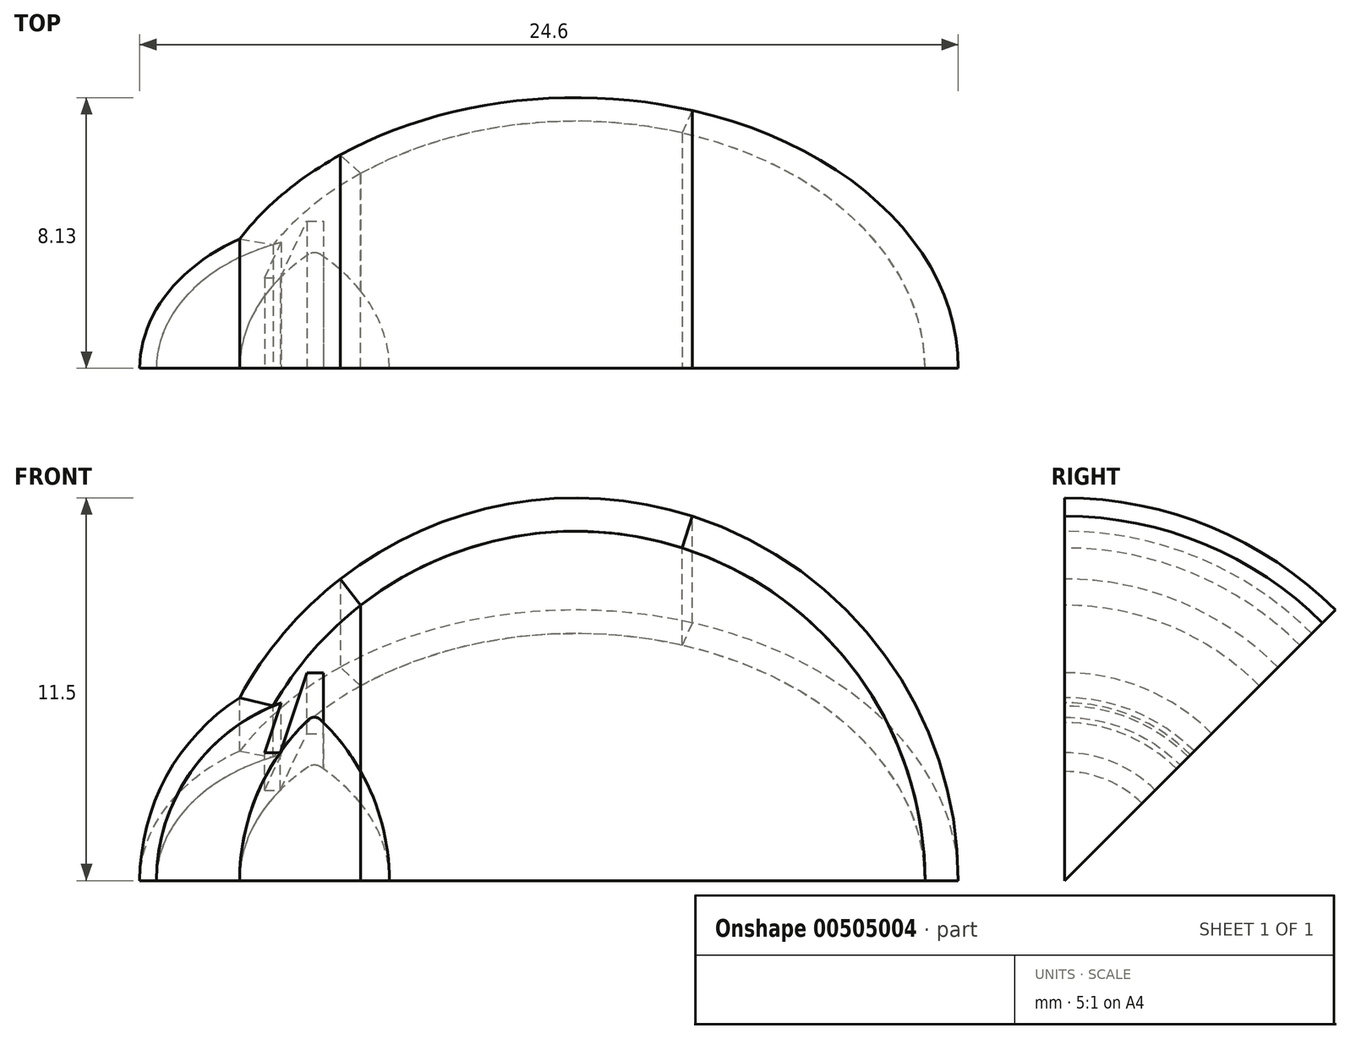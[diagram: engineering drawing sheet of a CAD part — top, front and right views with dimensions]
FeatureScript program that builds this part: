
annotation { "Feature Type Name" : "Feature", "Feature Type Description" : "" }
export const myFeature = defineFeature(function(context is Context, id is Id, definition is map)
    precondition{}
    {
        {
            var Q0;
            Q0=qCreatedBy(makeId("Front.planeOp"),FACE);
            var sketch = newSketch(context, id + "F0", { "sketchPlane" : qUnion([Q0])});
            skArc(sketch, "E0", {"start": v(11.5, 0) * mm, "mid": v(2.84, 11.14) * mm, "end": v(-10.1, 5.5) * mm});
            skLineSegment(sketch, "E1", {"start": v(11.5, 0) * mm, "end": v(-11.5, 0) * mm});
            skArc(sketch, "E2", {"start": v(-10.1, 5.5) * mm, "mid": v(-12.3, 3.13) * mm, "end": v(-13.1, 0) * mm});
            skLineSegment(sketch, "E3", {"start": v(-11.5, 0) * mm, "end": v(-13.1, 0) * mm});
            skSolve(sketch);
        }
        {
            var Q0;
            Q0=qSketchRegion(id+"F0",true);
            var Q1;
            Q1=sQuery(id+"F0.wireOp",EDGE,"E1");
            revolve(context, id + "F1", {"entities" : qUnion([Q0]), "axis" : qUnion([Q1]), "revolveType" : RevolveType.ONE_DIRECTION, "angle" : 45 * degree});
        }
        {
            var Q0;
            Q0=qCreatedBy(makeId("Front.planeOp"),FACE);
            var sketch = newSketch(context, id + "F2", { "sketchPlane" : qUnion([Q0])});
            skLineSegment(sketch, "E4", {"start": v(-10.1, 5.5) * mm, "end": v(-9.1, 5.25) * mm});
            skLineSegment(sketch, "E5", {"start": v(11.5, 0) * mm, "end": v(10.5, 0) * mm});
            skArc(sketch, "E6", {"start": v(10.5, 0) * mm, "mid": v(2.72, 10.14) * mm, "end": v(-9.1, 5.25) * mm});
            skArc(sketch, "E7", {"start": v(11.5, 0) * mm, "mid": v(2.84, 11.14) * mm, "end": v(-10.1, 5.5) * mm});
            skSolve(sketch);
        }
        {
            var Q0;
            Q0=makeQuery(id+"F2.imprint","IMPRINT",FACE,{"disambiguationData":[TD([[makeQuery(id+"F2.imprint","IMPRINT",EDGE,{"derivedFrom":sQuery(id+"F2.wireOp",EDGE,"E4")}),1.0]])]});
            var Q1;
            Q1=sQuery(id+"F2.wireOp",EDGE,"E6");
            var Q2;
            Q2=sQuery(id+"F2.wireOp",EDGE,"E4");
            var Q3;
            Q3=sQuery(id+"F0.wireOp",EDGE,"E1");
            revolve(context, id + "F3", {"operationType" : NewBodyOperationType.REMOVE, "entities" : qUnion([Q0]), "surfaceEntities" : qUnion([Q1, Q2]), "axis" : qUnion([Q3]), "revolveType" : RevolveType.ONE_DIRECTION, "angle" : 45 * degree});
        }
        {
            var Q0;
            Q0=qSketchRegion(id+"F2",true);
            var Q1;
            Q1=sQuery(id+"F0.wireOp",EDGE,"E1");
            revolve(context, id + "F4", {"entities" : qUnion([Q0]), "axis" : qUnion([Q1]), "revolveType" : RevolveType.ONE_DIRECTION, "angle" : 45 * degree});
        }
        {
            var Q0;
            Q0=makeQuery(id+"F0.imprint","IMPRINT",FACE,{"disambiguationData":[TD([[makeQuery(id+"F0.imprint","IMPRINT",EDGE,{"derivedFrom":sQuery(id+"F0.wireOp",EDGE,"E0")}),1.0]])]});
            var sketch = newSketch(context, id + "F5", { "sketchPlane" : qUnion([Q0])});
            skArc(sketch, "E8", {"start": v(-9.1, 5.25) * mm, "mid": v(-11.64, 3.16) * mm, "end": v(-12.6, 0) * mm});
            skLineSegment(sketch, "E9", {"start": v(-10.1, 5.5) * mm, "end": v(-9.1, 5.25) * mm});
            skLineSegment(sketch, "E10", {"start": v(-13.1, 0) * mm, "end": v(-12.6, 0) * mm});
            skArc(sketch, "E11", {"start": v(-10.1, 5.5) * mm, "mid": v(-12.3, 3.13) * mm, "end": v(-13.1, 0) * mm});
            skSolve(sketch);
        }
        {
            var Q0;
            Q0=qSketchRegion(id+"F5",true);
            var Q1;
            Q1=sQuery(id+"F5.wireOp",EDGE,"E8");
            var Q2;
            Q2=sQuery(id+"F5.wireOp",EDGE,"E9");
            var Q3;
            Q3=sQuery(id+"F0.wireOp",EDGE,"E3");
            revolve(context, id + "F6", {"operationType" : NewBodyOperationType.REMOVE, "entities" : qUnion([Q0]), "surfaceEntities" : qUnion([Q1, Q2]), "axis" : qUnion([Q3]), "revolveType" : RevolveType.ONE_DIRECTION, "angle" : 45 * degree});
        }
        {
            var Q0;
            Q0=qSketchRegion(id+"F5",true);
            var Q1;
            Q1=sQuery(id+"F0.wireOp",EDGE,"E1");
            revolve(context, id + "F7", {"entities" : qUnion([Q0]), "axis" : qUnion([Q1]), "revolveType" : RevolveType.ONE_DIRECTION, "angle" : 45 * degree});
        }
        {
            var Q0;
            Q0=qCreatedBy(makeId("Front.planeOp"),FACE);
            var sketch = newSketch(context, id + "F8", { "sketchPlane" : qUnion([Q0])});
            skArc(sketch, "E12", {"start": v(10, 0) * mm, "mid": v(8.28, 6.14) * mm, "end": v(3.2, 10) * mm});
            skLineSegment(sketch, "E13", {"start": v(10, 0) * mm, "end": v(10.5, 0) * mm});
            skArc(sketch, "E14", {"start": v(10.5, 0) * mm, "mid": v(8.48, 6.2) * mm, "end": v(3.2, 10) * mm});
            skSolve(sketch);
        }
        {
            var Q0;
            Q0=qSketchRegion(id+"F8",true);
            var Q1;
            Q1=sQuery(id+"F8.wireOp",EDGE,"E12");
            var Q2;
            Q2=sQuery(id+"F0.wireOp",EDGE,"E1");
            revolve(context, id + "F9", {"operationType" : NewBodyOperationType.REMOVE, "entities" : qUnion([Q0]), "surfaceEntities" : qUnion([Q1]), "axis" : qUnion([Q2]), "revolveType" : RevolveType.ONE_DIRECTION, "angle" : 45 * degree});
        }
        {
            var Q0;
            Q0=qSketchRegion(id+"F8",true);
            var Q1;
            Q1=sQuery(id+"F8.wireOp",EDGE,"E13");
            revolve(context, id + "F10", {"entities" : qUnion([Q0]), "axis" : qUnion([Q1]), "revolveType" : RevolveType.ONE_DIRECTION, "oppositeDirection" : true, "angle" : 45 * degree});
        }
        {
            var Q0;
            Q0=makeQuery(id+"F0.imprint","IMPRINT",FACE,{"disambiguationData":[TD([[makeQuery(id+"F0.imprint","IMPRINT",EDGE,{"derivedFrom":sQuery(id+"F0.wireOp",EDGE,"E0")}),1.0]])]});
            var sketch = newSketch(context, id + "F11", { "sketchPlane" : qUnion([Q0])});
            skLineSegment(sketch, "E15", {"start": v(8.35, 0) * mm, "end": v(9.86, 0) * mm});
            skLineSegment(sketch, "E16", {"start": v(9.86, 0) * mm, "end": v(9.86, 2.23) * mm});
            skLineSegment(sketch, "E17", {"start": v(9.86, 2.23) * mm, "end": v(8.35, 2.23) * mm});
            skLineSegment(sketch, "E18", {"start": v(8.35, 2.23) * mm, "end": v(8.35, 0) * mm});
            skSolve(sketch);
        }
        {
            var Q0;
            Q0=qSketchRegion(id+"F11",true);
            var Q1;
            Q1=sQuery(id+"F11.wireOp",EDGE,"E15");
            revolve(context, id + "F12", {"operationType" : NewBodyOperationType.REMOVE, "entities" : qUnion([Q0]), "axis" : qUnion([Q1]), "revolveType" : RevolveType.ONE_DIRECTION, "oppositeDirection" : true, "angle" : 45 * degree});
        }
        {
            var Q0;
            Q0=qSketchRegion(id+"F11",true);
            var Q1;
            Q1=sQuery(id+"F0.wireOp",EDGE,"E1");
            revolve(context, id + "F13", {"entities" : qUnion([Q0]), "axis" : qUnion([Q1]), "revolveType" : RevolveType.ONE_DIRECTION, "angle" : 45 * degree});
        }
        {
            var Q0;
            Q0=qCreatedBy(makeId("Front.planeOp"),FACE);
            var sketch = newSketch(context, id + "F14", { "sketchPlane" : qUnion([Q0])});
            skLineSegment(sketch, "E19", {"start": v(9.86, 2.23) * mm, "end": v(9.86, 0) * mm});
            skLineSegment(sketch, "E20", {"start": v(9.86, 0) * mm, "end": v(10, 0) * mm});
            skArc(sketch, "E21", {"start": v(10, 0) * mm, "mid": v(10, 1.12) * mm, "end": v(9.86, 2.23) * mm});
            skSolve(sketch);
        }
        {
            var Q0;
            Q0=qSketchRegion(id+"F14",true);
            var Q1;
            Q1=sQuery(id+"F14.wireOp",EDGE,"E20");
            revolve(context, id + "F15", {"operationType" : NewBodyOperationType.REMOVE, "entities" : qUnion([Q0]), "axis" : qUnion([Q1]), "revolveType" : RevolveType.ONE_DIRECTION, "oppositeDirection" : true, "angle" : 45 * degree});
        }
        {
            var Q0;
            Q0=qSketchRegion(id+"F14",true);
            var Q1;
            Q1=sQuery(id+"F0.wireOp",EDGE,"E1");
            revolve(context, id + "F16", {"operationType" : NewBodyOperationType.ADD, "entities" : qUnion([Q0]), "axis" : qUnion([Q1]), "revolveType" : RevolveType.ONE_DIRECTION, "angle" : 45 * degree});
        }
        {
            var Q0;
            Q0=qCreatedBy(makeId("Front.planeOp"),FACE);
            var sketch = newSketch(context, id + "F17", { "sketchPlane" : qUnion([Q0])});
            skLineSegment(sketch, "E22", {"start": v(3.5, 10.95) * mm, "end": v(3.2, 10) * mm});
            skArc(sketch, "E23", {"start": v(10.5, 0) * mm, "mid": v(8.48, 6.2) * mm, "end": v(3.2, 10) * mm});
            skArc(sketch, "E24", {"start": v(11.5, 0) * mm, "mid": v(9.29, 6.78) * mm, "end": v(3.5, 10.95) * mm});
            skLineSegment(sketch, "E25", {"start": v(10.5, 0) * mm, "end": v(11.5, 0) * mm});
            skSolve(sketch);
        }
        {
            var Q0;
            Q0=qSketchRegion(id+"F17",true);
            var Q1;
            Q1=sQuery(id+"F17.wireOp",EDGE,"E25");
            revolve(context, id + "F18", {"operationType" : NewBodyOperationType.REMOVE, "entities" : qUnion([Q0]), "axis" : qUnion([Q1]), "revolveType" : RevolveType.FULL, "oppositeDirection" : true});
        }
        {
            var Q0;
            Q0=qSketchRegion(id+"F17",true);
            var Q1;
            Q1=sQuery(id+"F0.wireOp",EDGE,"E1");
            revolve(context, id + "F19", {"entities" : qUnion([Q0]), "axis" : qUnion([Q1]), "revolveType" : RevolveType.ONE_DIRECTION, "angle" : 45 * degree});
        }
        {
            var Q0;
            Q0=qCreatedBy(makeId("Front.planeOp"),FACE);
            var sketch = newSketch(context, id + "F20", { "sketchPlane" : qUnion([Q0])});
            skArc(sketch, "E26", {"start": v(-8.85, 5.34) * mm, "mid": v(-11.57, 3.26) * mm, "end": v(-12.6, 0) * mm});
            skLineSegment(sketch, "E27", {"start": v(-8.85, 5.34) * mm, "end": v(-9.35, 3.84) * mm});
            skLineSegment(sketch, "E28", {"start": v(-9.35, 3.84) * mm, "end": v(-8.85, 3.84) * mm});
            skLineSegment(sketch, "E29", {"start": v(-12.6, 0) * mm, "end": v(-8.85, 0) * mm});
            skLineSegment(sketch, "E30", {"start": v(-8.85, 3.84) * mm, "end": v(-8.85, 0) * mm});
            skSolve(sketch);
        }
        {
            var Q0;
            Q0=qSketchRegion(id+"F20",true);
            var Q1;
            Q1=sQuery(id+"F20.wireOp",EDGE,"E29");
            revolve(context, id + "F21", {"operationType" : NewBodyOperationType.REMOVE, "entities" : qUnion([Q0]), "axis" : qUnion([Q1]), "revolveType" : RevolveType.FULL, "oppositeDirection" : true});
        }
        {
            var Q0;
            Q0=qSketchRegion(id+"F20",true);
            var Q1;
            Q1=sQuery(id+"F0.wireOp",EDGE,"E1");
            revolve(context, id + "F22", {"entities" : qUnion([Q0]), "axis" : qUnion([Q1]), "revolveType" : RevolveType.ONE_DIRECTION, "angle" : 45 * degree});
        }
        {
            var Q0;
            Q0=qCreatedBy(makeId("Front.planeOp"),FACE);
            var sketch = newSketch(context, id + "F23", { "sketchPlane" : qUnion([Q0])});
            skLineSegment(sketch, "E31", {"start": v(-5.6, 0) * mm, "end": v(-10.1, 0) * mm});
            skArc(sketch, "E32", {"start": v(-8.02, 4.84) * mm, "mid": v(-9.56, 2.63) * mm, "end": v(-10.1, 0) * mm});
            skLineSegment(sketch, "E33", {"start": v(-8.1, 0) * mm, "end": v(-8.1, 4.77) * mm, "construction": true});
            skArc(sketch, "E34", {"start": v(-5.6, 0) * mm, "mid": v(-6.14, 2.63) * mm, "end": v(-7.68, 4.84) * mm});
            skPoint(sketch, "E35.visualSharp", {"position": v(-7.85, 5) * mm});
            skArc(sketch, "E35.filletArc", {"start": v(-7.68, 4.84) * mm, "mid": v(-7.85, 4.91) * mm, "end": v(-8.02, 4.84) * mm});
            skSolve(sketch);
        }
        {
            var Q0;
            Q0=qSketchRegion(id+"F23",true);
            var Q1;
            Q1=sQuery(id+"F0.wireOp",EDGE,"E1");
            revolve(context, id + "F24", {"operationType" : NewBodyOperationType.REMOVE, "entities" : qUnion([Q0]), "axis" : qUnion([Q1]), "revolveType" : RevolveType.FULL, "oppositeDirection" : true});
        }
        {
            var Q0;
            Q0=qSketchRegion(id+"F23",true);
            var Q1;
            Q1=sQuery(id+"F0.wireOp",EDGE,"E1");
            revolve(context, id + "F25", {"entities" : qUnion([Q0]), "axis" : qUnion([Q1]), "revolveType" : RevolveType.ONE_DIRECTION, "angle" : 45 * degree});
        }
        {
            var Q0;
            Q0=qCreatedBy(makeId("Front.planeOp"),FACE);
            var sketch = newSketch(context, id + "F26", { "sketchPlane" : qUnion([Q0])});
            skLineSegment(sketch, "E36", {"start": v(-9.35, 3.84) * mm, "end": v(-8.88, 3.84) * mm});
            skLineSegment(sketch, "E37", {"start": v(-8.88, 3.84) * mm, "end": v(-8.08, 6.25) * mm});
            skLineSegment(sketch, "E38", {"start": v(-8.08, 6.25) * mm, "end": v(-7.58, 6.25) * mm});
            skLineSegment(sketch, "E39", {"start": v(-7.58, 6.25) * mm, "end": v(-7.58, 4.75) * mm});
            skLineSegment(sketch, "E40", {"start": v(-6.46, 3.28) * mm, "end": v(-6.46, 8.28) * mm});
            skLineSegment(sketch, "E41", {"start": v(-9.35, 3.84) * mm, "end": v(-8.85, 5.34) * mm});
            skArc(sketch, "E42", {"start": v(-6.46, 8.28) * mm, "mid": v(-7.92, 6.9) * mm, "end": v(-9.1, 5.25) * mm});
            skArc(sketch, "E43", {"start": v(-8.85, 5.34) * mm, "mid": v(-8.97, 5.3) * mm, "end": v(-9.1, 5.25) * mm});
            skArc(sketch, "E44", {"start": v(-6.46, 3.28) * mm, "mid": v(-6.97, 4.05) * mm, "end": v(-7.58, 4.75) * mm});
            skSolve(sketch);
        }
        {
            var Q0;
            Q0=qSketchRegion(id+"F26",true);
            var Q1;
            Q1=sQuery(id+"F23.wireOp",EDGE,"E31");
            revolve(context, id + "F27", {"operationType" : NewBodyOperationType.REMOVE, "entities" : qUnion([Q0]), "axis" : qUnion([Q1]), "revolveType" : RevolveType.FULL, "oppositeDirection" : true});
        }
        {
            var Q0;
            Q0=qSketchRegion(id+"F26",true);
            var Q1;
            Q1=sQuery(id+"F23.wireOp",EDGE,"E31");
            revolve(context, id + "F28", {"entities" : qUnion([Q0]), "axis" : qUnion([Q1]), "revolveType" : RevolveType.ONE_DIRECTION, "angle" : 45 * degree});
        }
        {
            var Q0;
            Q0=qCreatedBy(makeId("Front.planeOp"),FACE);
            var sketch = newSketch(context, id + "F29", { "sketchPlane" : qUnion([Q0])});
            skLineSegment(sketch, "E45", {"start": v(-6.46, 8.28) * mm, "end": v(-7.07, 9.07) * mm});
            skArc(sketch, "E46", {"start": v(-7.07, 9.07) * mm, "mid": v(-8.77, 7.44) * mm, "end": v(-10.1, 5.5) * mm});
            skArc(sketch, "E47", {"start": v(-6.46, 8.28) * mm, "mid": v(-7.92, 6.9) * mm, "end": v(-9.1, 5.25) * mm});
            skPoint(sketch, "E47.second.point", {"position": v(-9.1, 5.25) * mm});
            skPoint(sketch, "E47.third.point", {"position": v(-6.46, 8.28) * mm});
            skLineSegment(sketch, "E48", {"start": v(-10.1, 5.5) * mm, "end": v(-9.1, 5.25) * mm});
            skSolve(sketch);
        }
        {
            var Q0;
            Q0=qSketchRegion(id+"F29",true);
            var Q1;
            Q1=sQuery(id+"F23.wireOp",EDGE,"E31");
            revolve(context, id + "F30", {"operationType" : NewBodyOperationType.REMOVE, "entities" : qUnion([Q0]), "axis" : qUnion([Q1]), "revolveType" : RevolveType.FULL, "oppositeDirection" : true});
        }
        {
            var Q0;
            Q0=qSketchRegion(id+"F29",true);
            var Q1;
            Q1=sQuery(id+"F23.wireOp",EDGE,"E31");
            revolve(context, id + "F31", {"entities" : qUnion([Q0]), "axis" : qUnion([Q1]), "revolveType" : RevolveType.ONE_DIRECTION, "angle" : 45 * degree});
        }
        {
            var Q0;
            Q0=qCreatedBy(makeId("Front.planeOp"),FACE);
            var sketch = newSketch(context, id + "F32", { "sketchPlane" : qUnion([Q0])});
            skLineSegment(sketch, "E49", {"start": v(-6.46, 0) * mm, "end": v(-5.6, 0) * mm});
            skLineSegment(sketch, "E50", {"start": v(-6.46, 0) * mm, "end": v(-6.46, 3.28) * mm});
            skArc(sketch, "E51", {"start": v(-5.6, 0) * mm, "mid": v(-5.82, 1.7) * mm, "end": v(-6.46, 3.28) * mm});
            skPoint(sketch, "E51.third.point", {"position": v(-5.6, 0) * mm});
            skSolve(sketch);
        }
        {
            var Q0;
            Q0 = qSketchRegion(id + "F32", true);
            var Q1;
            Q1=sQuery(id+"F32.wireOp",EDGE,"E49");
            revolve(context, id + "F33", {"operationType" : NewBodyOperationType.REMOVE, "entities" : qUnion([Q0]), "axis" : qUnion([Q1]), "revolveType" : RevolveType.FULL, "oppositeDirection" : true});
        }
        {
            var Q0;
            Q0 = qSketchRegion(id + "F32", true);
            var Q1;
            Q1=sQuery(id+"F23.wireOp",EDGE,"E31");
            revolve(context, id + "F34", {"entities" : qUnion([Q0]), "axis" : qUnion([Q1]), "revolveType" : RevolveType.ONE_DIRECTION, "angle" : 45 * degree});
        }
    });
